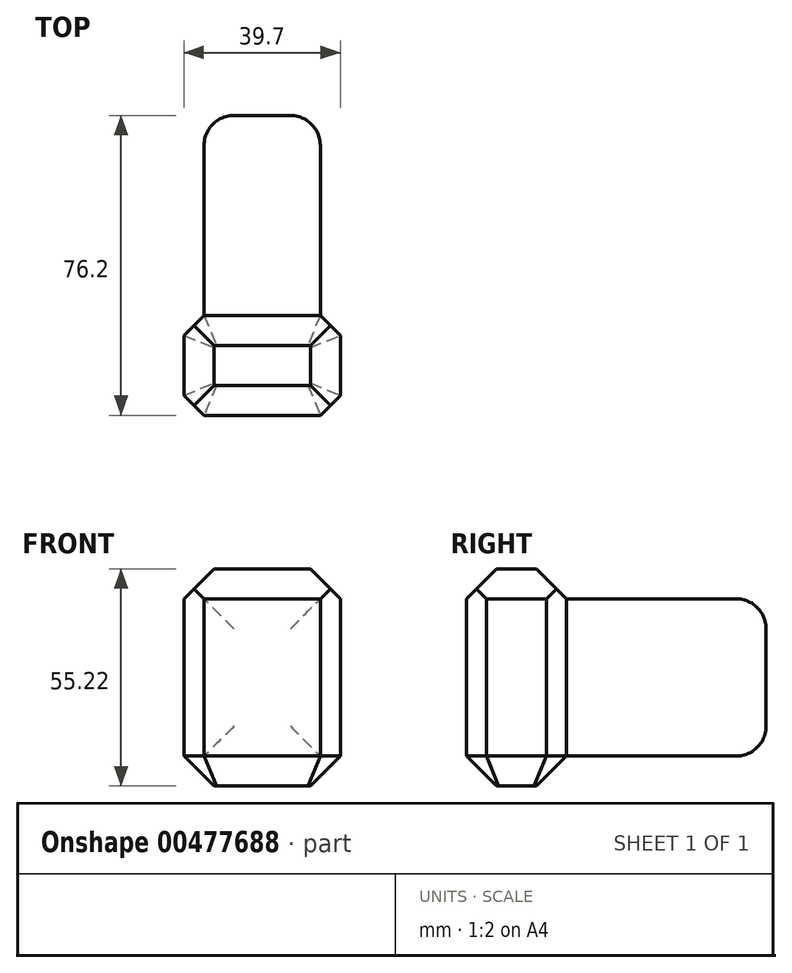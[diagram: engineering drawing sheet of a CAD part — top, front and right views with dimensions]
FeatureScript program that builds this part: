
annotation { "Feature Type Name" : "Feature", "Feature Type Description" : "" }
export const myFeature = defineFeature(function(context is Context, id is Id, definition is map)
    precondition{}
    {
        {
            var Q0;
            Q0=qCreatedBy(makeId("Front.planeOp"),FACE);
            var sketch = newSketch(context, id + "F0", { "sketchPlane" : qUnion([Q0])});
            skLineSegment(sketch, "E0.bottom", {"start": v(0, 0) * mm, "end": v(39.7, 0) * mm});
            skLineSegment(sketch, "E0.top", {"start": v(0, 55.22) * mm, "end": v(39.7, 55.22) * mm});
            skLineSegment(sketch, "E0.left", {"start": v(0, 0) * mm, "end": v(0, 55.22) * mm});
            skLineSegment(sketch, "E0.right", {"start": v(39.7, 0) * mm, "end": v(39.7, 55.22) * mm});
            skPoint(sketch, "E0.middle", {"position": v(19.85, 27.6) * mm});
            skSolve(sketch);
        }
        {
            var Q0;
            Q0=makeQuery(id+"F0.imprint","IMPRINT",FACE,{"disambiguationData":[TD([[makeQuery(id+"F0.imprint","IMPRINT",EDGE,{"derivedFrom":sQuery(id+"F0.wireOp",EDGE,"E0.bottom")}),1.0]])]});
            extrude(context, id + "F1", {"entities" : qUnion([Q0]), "depth" : 25.4 * mm});
        }
        {
            var Q0;
            Q0=makeQuery(id+"F1.opExtrude","CAP_EDGE",EDGE,{"disambiguationData":[OSD([sQuery(id+"F0.wireOp",EDGE,"E0.top")])],"isStart":false});
            var Q1;
            Q1=makeQuery(id+"F1.opExtrude","SWEPT_EDGE",EDGE,{"disambiguationData":[OSD([sQuery(id+"F0.wireOp",EDGE,"E0.top"),sQuery(id+"F0.wireOp",EDGE,"E0.left")])]});
            var Q2;
            Q2=makeQuery(id+"F1.opExtrude","SWEPT_EDGE",EDGE,{"disambiguationData":[OSD([sQuery(id+"F0.wireOp",EDGE,"E0.top"),sQuery(id+"F0.wireOp",EDGE,"E0.right")])]});
            var Q3;
            Q3=makeQuery(id+"F1.opExtrude","CAP_EDGE",EDGE,{"disambiguationData":[OSD([sQuery(id+"F0.wireOp",EDGE,"E0.top")])],"isStart":true});
            chamfer(context, id + "F2", {"entities" : qUnion([Q0, Q1, Q2, Q3]), "width" : 7.62 * mm, "tangentPropagation" : true});
        }
        {
            var Q0;
            Q0=makeQuery(id+"F1.opExtrude","CAP_EDGE",EDGE,{"disambiguationData":[OSD([sQuery(id+"F0.wireOp",EDGE,"E0.right")])],"isStart":true});
            var Q1;
            Q1=makeQuery(id+"F1.opExtrude","CAP_EDGE",EDGE,{"disambiguationData":[OSD([sQuery(id+"F0.wireOp",EDGE,"E0.left")])],"isStart":false});
            var Q2;
            Q2=makeQuery(id+"F1.opExtrude","CAP_EDGE",EDGE,{"disambiguationData":[OSD([sQuery(id+"F0.wireOp",EDGE,"E0.right")])],"isStart":false});
            var Q3;
            Q3=makeQuery(id+"F1.opExtrude","CAP_EDGE",EDGE,{"disambiguationData":[OSD([sQuery(id+"F0.wireOp",EDGE,"E0.left")])],"isStart":true});
            chamfer(context, id + "F3", {"entities" : qUnion([Q0, Q1, Q2, Q3]), "width" : 5.08 * mm, "tangentPropagation" : true});
        }
        {
            var Q0;
            Q0=makeQuery(id+"F3.opChamfer","BLEND_EDGE",EDGE,{"blendedFrom":[makeQuery(id+"F1.opExtrude","CAP_EDGE",EDGE,{"disambiguationData":[OSD([sQuery(id+"F0.wireOp",EDGE,"E0.left")])],"isStart":true}),makeQuery(id+"F1.opExtrude","SWEPT_FACE",FACE,{"disambiguationData":[OSD([sQuery(id+"F0.wireOp",EDGE,"E0.bottom")])]})],"blendedInto":[makeQuery(id+"F1.opExtrude","SWEPT_FACE",FACE,{"disambiguationData":[OSD([sQuery(id+"F0.wireOp",EDGE,"E0.bottom")])]})]});
            var Q1;
            Q1=makeQuery(id+"F1.opExtrude","SWEPT_EDGE",EDGE,{"disambiguationData":[OSD([sQuery(id+"F0.wireOp",EDGE,"E0.bottom"),sQuery(id+"F0.wireOp",EDGE,"E0.right")])]});
            var Q2;
            Q2=makeQuery(id+"F1.opExtrude","SWEPT_EDGE",EDGE,{"disambiguationData":[OSD([sQuery(id+"F0.wireOp",EDGE,"E0.bottom"),sQuery(id+"F0.wireOp",EDGE,"E0.left")])]});
            var Q3;
            Q3=makeQuery(id+"F3.opChamfer","BLEND_EDGE",EDGE,{"blendedFrom":[makeQuery(id+"F1.opExtrude","CAP_EDGE",EDGE,{"disambiguationData":[OSD([sQuery(id+"F0.wireOp",EDGE,"E0.left")])],"isStart":false}),makeQuery(id+"F1.opExtrude","SWEPT_FACE",FACE,{"disambiguationData":[OSD([sQuery(id+"F0.wireOp",EDGE,"E0.bottom")])]})],"blendedInto":[makeQuery(id+"F1.opExtrude","SWEPT_FACE",FACE,{"disambiguationData":[OSD([sQuery(id+"F0.wireOp",EDGE,"E0.bottom")])]})]});
            var Q4;
            Q4=makeQuery(id+"F1.opExtrude","CAP_EDGE",EDGE,{"disambiguationData":[OSD([sQuery(id+"F0.wireOp",EDGE,"E0.bottom")])],"isStart":false});
            var Q5;
            Q5=makeQuery(id+"F1.opExtrude","CAP_EDGE",EDGE,{"disambiguationData":[OSD([sQuery(id+"F0.wireOp",EDGE,"E0.bottom")])],"isStart":true});
            var Q6;
            Q6=makeQuery(id+"F3.opChamfer","BLEND_EDGE",EDGE,{"blendedFrom":[makeQuery(id+"F1.opExtrude","CAP_EDGE",EDGE,{"disambiguationData":[OSD([sQuery(id+"F0.wireOp",EDGE,"E0.right")])],"isStart":true}),makeQuery(id+"F1.opExtrude","SWEPT_FACE",FACE,{"disambiguationData":[OSD([sQuery(id+"F0.wireOp",EDGE,"E0.bottom")])]})],"blendedInto":[makeQuery(id+"F1.opExtrude","SWEPT_FACE",FACE,{"disambiguationData":[OSD([sQuery(id+"F0.wireOp",EDGE,"E0.bottom")])]})]});
            var Q7;
            Q7=makeQuery(id+"F3.opChamfer","BLEND_EDGE",EDGE,{"blendedFrom":[makeQuery(id+"F1.opExtrude","CAP_EDGE",EDGE,{"disambiguationData":[OSD([sQuery(id+"F0.wireOp",EDGE,"E0.right")])],"isStart":false}),makeQuery(id+"F1.opExtrude","SWEPT_FACE",FACE,{"disambiguationData":[OSD([sQuery(id+"F0.wireOp",EDGE,"E0.bottom")])]})],"blendedInto":[makeQuery(id+"F1.opExtrude","SWEPT_FACE",FACE,{"disambiguationData":[OSD([sQuery(id+"F0.wireOp",EDGE,"E0.bottom")])]})]});
            chamfer(context, id + "F4", {"entities" : qUnion([Q0, Q1, Q2, Q3, Q4, Q5, Q6, Q7]), "width" : 7.62 * mm, "tangentPropagation" : true});
        }
        {
            var Q0;
            Q0=makeQuery(id+"F1.opExtrude","CAP_FACE",FACE,{"disambiguationData":[OSD([sQuery(id+"F0.wireOp",EDGE,"E0.bottom"),sQuery(id+"F0.wireOp",EDGE,"E0.top"),sQuery(id+"F0.wireOp",EDGE,"E0.left"),sQuery(id+"F0.wireOp",EDGE,"E0.right")])],"isStart":true});
            extrude(context, id + "F5", {"entities" : qUnion([Q0]), "operationType" : NewBodyOperationType.ADD, "depth" : 50.8 * mm});
        }
        {
            var Q0;
            {var subQ0=sQuery(id+"F0.wireOp",EDGE,"E0.right");var subQ1=sQuery(id+"F0.wireOp",EDGE,"E0.left");var subQ2=sQuery(id+"F0.wireOp",EDGE,"E0.top");var subQ3=sQuery(id+"F0.wireOp",EDGE,"E0.bottom");Q0=makeQuery(id+"F5.opExtrude","CAP_EDGE",EDGE,{"disambiguationData":[OSD([subQ3,subQ2,subQ1,subQ0]),TDD([makeQuery(id+"F3.opChamfer","BLEND_EDGE",EDGE,{"blendedFrom":[makeQuery(id+"F1.opExtrude","CAP_EDGE",EDGE,{"disambiguationData":[OSD([subQ0])],"isStart":true}),makeQuery(id+"F1.opExtrude","CAP_FACE",FACE,{"disambiguationData":[OSD([subQ3,subQ2,subQ1,subQ0])],"isStart":true})],"blendedInto":[makeQuery(id+"F1.opExtrude","CAP_FACE",FACE,{"disambiguationData":[OSD([subQ3,subQ2,subQ1,subQ0])],"isStart":true})]})])],"isStart":false});}
            var Q1;
            {var subQ0=sQuery(id+"F0.wireOp",EDGE,"E0.right");var subQ1=sQuery(id+"F0.wireOp",EDGE,"E0.left");var subQ2=sQuery(id+"F0.wireOp",EDGE,"E0.top");var subQ3=sQuery(id+"F0.wireOp",EDGE,"E0.bottom");Q1=makeQuery(id+"F5.opExtrude","CAP_EDGE",EDGE,{"disambiguationData":[OSD([subQ3,subQ2,subQ1,subQ0]),TDD([makeQuery(id+"F2.opChamfer","BLEND_EDGE",EDGE,{"blendedFrom":[makeQuery(id+"F1.opExtrude","CAP_EDGE",EDGE,{"disambiguationData":[OSD([subQ2])],"isStart":true}),makeQuery(id+"F1.opExtrude","CAP_FACE",FACE,{"disambiguationData":[OSD([subQ3,subQ2,subQ1,subQ0])],"isStart":true})],"blendedInto":[makeQuery(id+"F1.opExtrude","CAP_FACE",FACE,{"disambiguationData":[OSD([subQ3,subQ2,subQ1,subQ0])],"isStart":true})]})])],"isStart":false});}
            var Q2;
            {var subQ0=sQuery(id+"F0.wireOp",EDGE,"E0.right");var subQ1=sQuery(id+"F0.wireOp",EDGE,"E0.left");var subQ2=sQuery(id+"F0.wireOp",EDGE,"E0.top");var subQ3=sQuery(id+"F0.wireOp",EDGE,"E0.bottom");Q2=makeQuery(id+"F5.opExtrude","CAP_EDGE",EDGE,{"disambiguationData":[OSD([subQ3,subQ2,subQ1,subQ0]),TDD([makeQuery(id+"F3.opChamfer","BLEND_EDGE",EDGE,{"blendedFrom":[makeQuery(id+"F1.opExtrude","CAP_EDGE",EDGE,{"disambiguationData":[OSD([subQ1])],"isStart":true}),makeQuery(id+"F1.opExtrude","CAP_FACE",FACE,{"disambiguationData":[OSD([subQ3,subQ2,subQ1,subQ0])],"isStart":true})],"blendedInto":[makeQuery(id+"F1.opExtrude","CAP_FACE",FACE,{"disambiguationData":[OSD([subQ3,subQ2,subQ1,subQ0])],"isStart":true})]})])],"isStart":false});}
            var Q3;
            {var subQ0=sQuery(id+"F0.wireOp",EDGE,"E0.right");var subQ1=sQuery(id+"F0.wireOp",EDGE,"E0.left");var subQ2=sQuery(id+"F0.wireOp",EDGE,"E0.top");var subQ3=sQuery(id+"F0.wireOp",EDGE,"E0.bottom");Q3=makeQuery(id+"F5.opExtrude","CAP_EDGE",EDGE,{"disambiguationData":[OSD([subQ3,subQ2,subQ1,subQ0]),TDD([makeQuery(id+"F4.opChamfer","BLEND_EDGE",EDGE,{"blendedFrom":[makeQuery(id+"F1.opExtrude","CAP_EDGE",EDGE,{"disambiguationData":[OSD([subQ3])],"isStart":true}),makeQuery(id+"F1.opExtrude","CAP_FACE",FACE,{"disambiguationData":[OSD([subQ3,subQ2,subQ1,subQ0])],"isStart":true})],"blendedInto":[makeQuery(id+"F1.opExtrude","CAP_FACE",FACE,{"disambiguationData":[OSD([subQ3,subQ2,subQ1,subQ0])],"isStart":true})]})])],"isStart":false});}
            fillet(context, id + "F6", {"entities" : qUnion([Q0, Q1, Q2, Q3]), "radius" : 7.62 * mm, "tangentPropagation" : true, "allowEdgeOverflow" : false});
        }
    });
